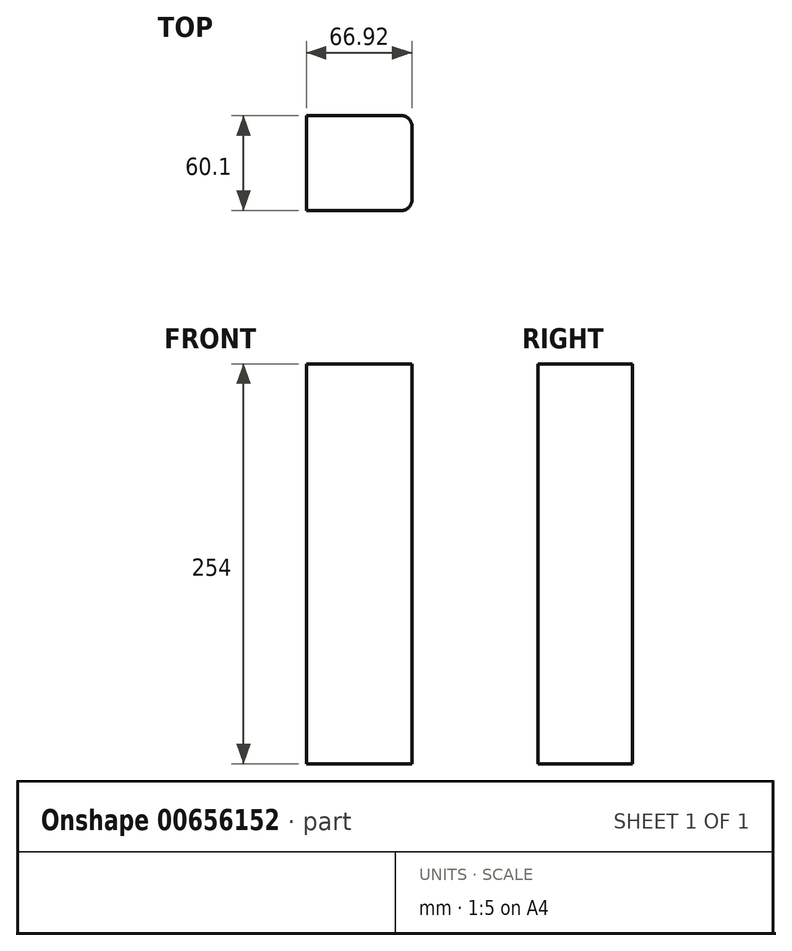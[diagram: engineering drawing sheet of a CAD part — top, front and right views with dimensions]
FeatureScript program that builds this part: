
annotation { "Feature Type Name" : "Feature", "Feature Type Description" : "" }
export const myFeature = defineFeature(function(context is Context, id is Id, definition is map)
    precondition{}
    {
        {
            var Q0;
            Q0=qCreatedBy(makeId("Top.planeOp"),FACE);
            var sketch = newSketch(context, id + "F0", { "sketchPlane" : qUnion([Q0])});
            skLineSegment(sketch, "E0", {"start": v(-26.64, 37.7) * mm, "end": v(33.93, 37.7) * mm});
            skLineSegment(sketch, "E1", {"start": v(40.28, 31.35) * mm, "end": v(40.28, -16.05) * mm});
            skLineSegment(sketch, "E2", {"start": v(33.93, -22.4) * mm, "end": v(-26.64, -22.4) * mm});
            skLineSegment(sketch, "E3", {"start": v(-26.64, -22.4) * mm, "end": v(-26.64, 37.7) * mm});
            skPoint(sketch, "E4.visualSharp", {"position": v(40.28, 37.7) * mm});
            skArc(sketch, "E4.filletArc", {"start": v(40.28, 31.35) * mm, "mid": v(38.42, 35.84) * mm, "end": v(33.93, 37.7) * mm});
            skPoint(sketch, "E5.visualSharp", {"position": v(40.28, -22.4) * mm});
            skArc(sketch, "E5.filletArc", {"start": v(33.93, -22.4) * mm, "mid": v(38.42, -20.54) * mm, "end": v(40.28, -16.05) * mm});
            skSolve(sketch);
        }
        {
            var Q0;
            Q0 = qSketchRegion(id + "F0", true);
            extrude(context, id + "F1", {"entities" : qUnion([Q0]), "depth" : 254 * mm, "offsetDistance" : 25.4 * mm});
        }
    });
